# Revit family: ROTHOB_Rothoblaas_Screw_VGZEvo
name_source: partatom
category: Collegamenti strutturali
units: mm (PartAtom-declared; Revit-internal decimal feet)

## family parameters
Attiva taglio nelle viste = Sì
Condiviso = No
Host = Superficie
Materiale per comportamento modello = Acciaio
Numero OmniClass = 23.13.23.11.19.13
Taglio con vuoti quando caricato = No
Titolo OmniClass = Wood Connectors

## types (44) — shared parameters
CECode = ETA-11/0030
Category = Pr_20_29_76_75: Self-tapping screws
CodePerformance = CE - Construction products
Color = Silver
Description = Fully threaded screw with cylindrical head
DurationUnit = Years
Esporta tipo in formato IFC con nome = IfcMechanicalFastenerType
ExpectedLife = 50
Features = Self-tapping screws for timber constructions
Finish = C4 EVO coating
HeadThickness = 7.2 mm  [stored 0.023622 ft]
ICC-ESCode = AC233 | AC257 ESR-4645
IfcExportAs = IfcMechanicalFastenerType
IfcExportType = USERDEFINED
ManufacturerName = ROTHO BLAAS SRL
ManufacturerURL = www.rothoblaas.com
Material = Carbon steel
ModelDisclaimer = The latest version of the data sheets can be found on our website
Name = Screw
ObjectMaterial = ROTHOB_Rothoblaas_CarbonSteel_C4EvoCoating
OmniClassCode = 23-13 23 11 19 13
OmniClassTitle = Wood Connectors
OmniClassVersion = 2012-05-16
ProductInformation = https://www.rothoblaas.com
Prospetto di default = 1219.2 mm
Shape = Cylindrical
Tipo IFC predefinito = USERDEFINED
UKCACode = UKTA-0836 22/6195
UniClass2015Code = Pr_20_29_76_75
UniClass2015Title = Self-tapping screws
UniClass2015Version = Products v1.30
Version = 1

## per-type parameters (varying)
| type | BitType | HeadDiameter_dk | InnerHeadDiameter | InsertionLength_L | MinWeight | ModelNumber | ModelNumberCode | NominalDiameter | NominalDiameter_d1 | NominalLength | Size | ThreadDiameter_d2 | ThreadLength_b | ThreadRadius | TipLength | UnderheadDiameter |
| 05.3x080mm | 25 | 8 mm  [stored 0.0262467 ft] | 4 mm  [stored 0.0131234 ft] | 80 mm | 0.01 kg | VGZEVO580 | 580 | 5.3 mm  [stored 0.0173885 ft] | 5.3 mm  [stored 0.0173885 ft] | 80 mm | 5.3x80 mm | 3.6 mm  [stored 0.011811 ft] | 70 mm | 1.8 mm  [stored 0.00590551 ft] | 4 mm  [stored 0.0131234 ft] | 7.2 mm  [stored 0.023622 ft] |
| 05.3x100mm | 25 | 8 mm  [stored 0.0262467 ft] | 4 mm  [stored 0.0131234 ft] | 100 mm | 0.008 kg | VGZEVO5100 | 5100 | 5.3 mm  [stored 0.0173885 ft] | 5.3 mm  [stored 0.0173885 ft] | 100 mm | 5.3x100 mm | 3.6 mm  [stored 0.011811 ft] | 90 mm | 1.8 mm  [stored 0.00590551 ft] | 5 mm  [stored 0.0164042 ft] | 7.2 mm  [stored 0.023622 ft] |
| 05.3x120mm | 25 | 8 mm  [stored 0.0262467 ft] | 4 mm  [stored 0.0131234 ft] | 120 mm | 0.010 kg | VGZEVO5120 | 5120 | 5.3 mm  [stored 0.0173885 ft] | 5.3 mm  [stored 0.0173885 ft] | 120 mm | 5.3x120 mm | 3.6 mm  [stored 0.011811 ft] | 110 mm | 1.8 mm  [stored 0.00590551 ft] | 6 mm  [stored 0.019685 ft] | 7.2 mm  [stored 0.023622 ft] |
| 05.6x140mm | 25 | 8 mm  [stored 0.0262467 ft] | 4 mm  [stored 0.0131234 ft] | 140 mm | 0.016 kg | VGZEVO5140 | 5140 | 5.6 mm  [stored 0.0183727 ft] | 5.6 mm  [stored 0.0183727 ft] | 140 mm | 5.6x140 mm | 3.8 mm | 130 mm | 1.9 mm | 7 mm  [stored 0.0229659 ft] | 7.2 mm  [stored 0.023622 ft] |
| 05.6x150mm | 25 | 8 mm  [stored 0.0262467 ft] | 4 mm  [stored 0.0131234 ft] | 150 mm | 0.018 kg | VGZEVO5150 | 5150 | 5.6 mm  [stored 0.0183727 ft] | 5.6 mm  [stored 0.0183727 ft] | 150 mm | 5.6x150 mm | 3.8 mm | 140 mm | 1.9 mm | 7.5 mm  [stored 0.0246063 ft] | 7.2 mm  [stored 0.023622 ft] |
| 05.6x160mm | 25 | 8 mm  [stored 0.0262467 ft] | 4 mm  [stored 0.0131234 ft] | 160 mm | 0.018 kg | VGZEVO5160 | 5160 | 5.6 mm  [stored 0.0183727 ft] | 5.6 mm  [stored 0.0183727 ft] | 160 mm | 5.6x160 mm | 3.8 mm | 150 mm | 1.9 mm | 8 mm  [stored 0.0262467 ft] | 7.2 mm  [stored 0.023622 ft] |
| 07x080mm | 30 | 9.5 mm  [stored 0.031168 ft] | 4.75 mm  [stored 0.015584 ft] | 80 mm | 0.015 kg | VGZEVO780 | 780 | 7 mm  [stored 0.0229659 ft] | 7 mm  [stored 0.0229659 ft] | 80 mm | 7x80 mm | 4.6 mm  [stored 0.0150919 ft] | 70 mm | 2.3 mm  [stored 0.00754593 ft] | 4 mm  [stored 0.0131234 ft] | 8.55 mm |
| 07x100mm | 30 | 9.5 mm  [stored 0.031168 ft] | 4.75 mm  [stored 0.015584 ft] | 100 mm | 0.019 kg | VGZEVO7100 | 7100 | 7 mm  [stored 0.0229659 ft] | 7 mm  [stored 0.0229659 ft] | 100 mm | 7x100 mm | 4.6 mm  [stored 0.0150919 ft] | 90 mm | 2.3 mm  [stored 0.00754593 ft] | 5 mm  [stored 0.0164042 ft] | 8.55 mm |
| 07x120mm | 30 | 9.5 mm  [stored 0.031168 ft] | 4.75 mm  [stored 0.015584 ft] | 120 mm | 0.016 kg | VGZEVO7120 | 7120 | 7 mm  [stored 0.0229659 ft] | 7 mm  [stored 0.0229659 ft] | 120 mm | 7x120 mm | 4.6 mm  [stored 0.0150919 ft] | 110 mm | 2.3 mm  [stored 0.00754593 ft] | 6 mm  [stored 0.019685 ft] | 8.55 mm |
| 07x140mm | 30 | 9.5 mm  [stored 0.031168 ft] | 4.75 mm  [stored 0.015584 ft] | 140 mm | 0.022 kg | VGZEVO7140 | 7140 | 7 mm  [stored 0.0229659 ft] | 7 mm  [stored 0.0229659 ft] | 140 mm | 7x140 mm | 4.6 mm  [stored 0.0150919 ft] | 130 mm | 2.3 mm  [stored 0.00754593 ft] | 7 mm  [stored 0.0229659 ft] | 8.55 mm |
| 07x160mm | 30 | 9.5 mm  [stored 0.031168 ft] | 4.75 mm  [stored 0.015584 ft] | 160 mm | 0.023 kg | VGZEVO7160 | 7160 | 7 mm  [stored 0.0229659 ft] | 7 mm  [stored 0.0229659 ft] | 160 mm | 7x160 mm | 4.6 mm  [stored 0.0150919 ft] | 150 mm | 2.3 mm  [stored 0.00754593 ft] | 8 mm  [stored 0.0262467 ft] | 8.55 mm |
| 07x180mm | 30 | 9.5 mm  [stored 0.031168 ft] | 4.75 mm  [stored 0.015584 ft] | 180 mm | 0.028 kg | VGZEVO7180 | 7180 | 7 mm  [stored 0.0229659 ft] | 7 mm  [stored 0.0229659 ft] | 180 mm | 7x180 mm | 4.6 mm  [stored 0.0150919 ft] | 170 mm | 2.3 mm  [stored 0.00754593 ft] | 9 mm  [stored 0.0295276 ft] | 8.55 mm |
| 07x200mm | 30 | 9.5 mm  [stored 0.031168 ft] | 4.75 mm  [stored 0.015584 ft] | 200 mm | 0.031 kg | VGZEVO7200 | 7200 | 7 mm  [stored 0.0229659 ft] | 7 mm  [stored 0.0229659 ft] | 200 mm | 7x200 mm | 4.6 mm  [stored 0.0150919 ft] | 190 mm | 2.3 mm  [stored 0.00754593 ft] | 10 mm  [stored 0.0328084 ft] | 8.55 mm |
| 07x220mm | 30 | 9.5 mm  [stored 0.031168 ft] | 4.75 mm  [stored 0.015584 ft] | 220 mm | 0.035 kg | VGZEVO7220 | 7220 | 7 mm  [stored 0.0229659 ft] | 7 mm  [stored 0.0229659 ft] | 220 mm | 7x220 mm | 4.6 mm  [stored 0.0150919 ft] | 210 mm | 2.3 mm  [stored 0.00754593 ft] | 11 mm  [stored 0.0360892 ft] | 8.55 mm |
| 07x240mm | 30 | 9.5 mm  [stored 0.031168 ft] | 4.75 mm  [stored 0.015584 ft] | 240 mm | 0.036 kg | VGZEVO7240 | 7240 | 7 mm  [stored 0.0229659 ft] | 7 mm  [stored 0.0229659 ft] | 240 mm | 7x240 mm | 4.6 mm  [stored 0.0150919 ft] | 230 mm | 2.3 mm  [stored 0.00754593 ft] | 12 mm  [stored 0.0393701 ft] | 8.55 mm |
| 07x260mm | 30 | 9.5 mm  [stored 0.031168 ft] | 4.75 mm  [stored 0.015584 ft] | 260 mm | 0.035 kg | VGZEVO7260 | 7260 | 7 mm  [stored 0.0229659 ft] | 7 mm  [stored 0.0229659 ft] | 260 mm | 7x260 mm | 4.6 mm  [stored 0.0150919 ft] | 250 mm | 2.3 mm  [stored 0.00754593 ft] | 13 mm | 8.55 mm |
| 07x280mm | 30 | 9.5 mm  [stored 0.031168 ft] | 4.75 mm  [stored 0.015584 ft] | 280 mm | 0.041 kg | VGZEVO7280 | 7280 | 7 mm  [stored 0.0229659 ft] | 7 mm  [stored 0.0229659 ft] | 280 mm | 7x280 mm | 4.6 mm  [stored 0.0150919 ft] | 270 mm | 2.3 mm  [stored 0.00754593 ft] | 14 mm  [stored 0.0459318 ft] | 8.55 mm |
| 07x300mm | 30 | 9.5 mm  [stored 0.031168 ft] | 4.75 mm  [stored 0.015584 ft] | 300 mm | 0.046 kg | VGZEVO7300 | 7300 | 7 mm  [stored 0.0229659 ft] | 7 mm  [stored 0.0229659 ft] | 300 mm | 7x300 mm | 4.6 mm  [stored 0.0150919 ft] | 290 mm | 2.3 mm  [stored 0.00754593 ft] | 15 mm  [stored 0.0492126 ft] | 8.55 mm |
| 07x340mm | 30 | 9.5 mm  [stored 0.031168 ft] | 4.75 mm  [stored 0.015584 ft] | 340 mm | 0.098 kg | VGZEVO7340 | 7340 | 7 mm  [stored 0.0229659 ft] | 7 mm  [stored 0.0229659 ft] | 340 mm | 7x340 mm | 4.6 mm  [stored 0.0150919 ft] | 330 mm | 2.3 mm  [stored 0.00754593 ft] | 17 mm | 8.55 mm |
| 07x380mm | 30 | 9.5 mm  [stored 0.031168 ft] | 4.75 mm  [stored 0.015584 ft] | 380 mm | 0.046 kg | VGZEVO7380 | 7380 | 7 mm  [stored 0.0229659 ft] | 7 mm  [stored 0.0229659 ft] | 380 mm | 7x380 mm | 4.6 mm  [stored 0.0150919 ft] | 370 mm | 2.3 mm  [stored 0.00754593 ft] | 19 mm | 8.55 mm |
| 09x160mm | 40 | 11.5 mm  [stored 0.0377297 ft] | 5.75 mm  [stored 0.0188648 ft] | 160 mm | 0.045 kg | VGZEVO9160 | 9160 | 9 mm  [stored 0.0295276 ft] | 9 mm  [stored 0.0295276 ft] | 160 mm | 9x160 mm | 5.9 mm  [stored 0.019357 ft] | 150 mm | 2.95 mm  [stored 0.00967848 ft] | 8 mm  [stored 0.0262467 ft] | 10.35 mm |
| 09x180mm | 40 | 11.5 mm  [stored 0.0377297 ft] | 5.75 mm  [stored 0.0188648 ft] | 180 mm | 0.05 kg | VGZEVO9180 | 9180 | 9 mm  [stored 0.0295276 ft] | 9 mm  [stored 0.0295276 ft] | 180 mm | 9x180 mm | 5.9 mm  [stored 0.019357 ft] | 170 mm | 2.95 mm  [stored 0.00967848 ft] | 9 mm  [stored 0.0295276 ft] | 10.35 mm |
| 09x200mm | 40 | 11.5 mm  [stored 0.0377297 ft] | 5.75 mm  [stored 0.0188648 ft] | 200 mm | 0.051 kg | VGZEVO9200 | 9200 | 9 mm  [stored 0.0295276 ft] | 9 mm  [stored 0.0295276 ft] | 200 mm | 9x200 mm | 5.9 mm  [stored 0.019357 ft] | 190 mm | 2.95 mm  [stored 0.00967848 ft] | 10 mm  [stored 0.0328084 ft] | 10.35 mm |
| 09x220mm | 40 | 11.5 mm  [stored 0.0377297 ft] | 5.75 mm  [stored 0.0188648 ft] | 220 mm | 0.060 kg | VGZEVO9220 | 9220 | 9 mm  [stored 0.0295276 ft] | 9 mm  [stored 0.0295276 ft] | 220 mm | 9x220 mm | 5.9 mm  [stored 0.019357 ft] | 210 mm | 2.95 mm  [stored 0.00967848 ft] | 11 mm  [stored 0.0360892 ft] | 10.35 mm |
| 09x240mm | 40 | 11.5 mm  [stored 0.0377297 ft] | 5.75 mm  [stored 0.0188648 ft] | 240 mm | 0.061 kg | VGZEVO9240 | 9240 | 9 mm  [stored 0.0295276 ft] | 9 mm  [stored 0.0295276 ft] | 240 mm | 9x240 mm | 5.9 mm  [stored 0.019357 ft] | 230 mm | 2.95 mm  [stored 0.00967848 ft] | 12 mm  [stored 0.0393701 ft] | 10.35 mm |
| 09x260mm | 40 | 11.5 mm  [stored 0.0377297 ft] | 5.75 mm  [stored 0.0188648 ft] | 260 mm | 0.069 kg | VGZEVO9260 | 9260 | 9 mm  [stored 0.0295276 ft] | 9 mm  [stored 0.0295276 ft] | 260 mm | 9x260 mm | 5.9 mm  [stored 0.019357 ft] | 250 mm | 2.95 mm  [stored 0.00967848 ft] | 13 mm | 10.35 mm |
| 09x280mm | 40 | 11.5 mm  [stored 0.0377297 ft] | 5.75 mm  [stored 0.0188648 ft] | 280 mm | 0.072 kg | VGZEVO9280 | 9280 | 9 mm  [stored 0.0295276 ft] | 9 mm  [stored 0.0295276 ft] | 280 mm | 9x280 mm | 5.9 mm  [stored 0.019357 ft] | 270 mm | 2.95 mm  [stored 0.00967848 ft] | 14 mm  [stored 0.0459318 ft] | 10.35 mm |
| 09x300mm | 40 | 11.5 mm  [stored 0.0377297 ft] | 5.75 mm  [stored 0.0188648 ft] | 300 mm | 0.073 kg | VGZEVO9300 | 9300 | 9 mm  [stored 0.0295276 ft] | 9 mm  [stored 0.0295276 ft] | 300 mm | 9x300 mm | 5.9 mm  [stored 0.019357 ft] | 290 mm | 2.95 mm  [stored 0.00967848 ft] | 15 mm  [stored 0.0492126 ft] | 10.35 mm |
| 09x320mm | 40 | 11.5 mm  [stored 0.0377297 ft] | 5.75 mm  [stored 0.0188648 ft] | 320 mm | 0.082 kg | VGZEVO9320 | 9320 | 9 mm  [stored 0.0295276 ft] | 9 mm  [stored 0.0295276 ft] | 320 mm | 9x320 mm | 5.9 mm  [stored 0.019357 ft] | 310 mm | 2.95 mm  [stored 0.00967848 ft] | 16 mm  [stored 0.0524934 ft] | 10.35 mm |
| 09x340mm | 40 | 11.5 mm  [stored 0.0377297 ft] | 5.75 mm  [stored 0.0188648 ft] | 340 mm | 0.098 kg | VGZEVO9340 | 9340 | 9 mm  [stored 0.0295276 ft] | 9 mm  [stored 0.0295276 ft] | 340 mm | 9x340 mm | 5.9 mm  [stored 0.019357 ft] | 330 mm | 2.95 mm  [stored 0.00967848 ft] | 17 mm | 10.35 mm |
| 09x360mm | 40 | 11.5 mm  [stored 0.0377297 ft] | 5.75 mm  [stored 0.0188648 ft] | 360 mm | 0.090 kg | VGZEVO9360 | 9360 | 9 mm  [stored 0.0295276 ft] | 9 mm  [stored 0.0295276 ft] | 360 mm | 9x360 mm | 5.9 mm  [stored 0.019357 ft] | 350 mm | 2.95 mm  [stored 0.00967848 ft] | 18 mm  [stored 0.0590551 ft] | 10.35 mm |
| 09x380mm | 40 | 11.5 mm  [stored 0.0377297 ft] | 5.75 mm  [stored 0.0188648 ft] | 380 mm | 0.095 kg | VGZEVO9380 | 9380 | 9 mm  [stored 0.0295276 ft] | 9 mm  [stored 0.0295276 ft] | 380 mm | 9x380 mm | 5.9 mm  [stored 0.019357 ft] | 370 mm | 2.95 mm  [stored 0.00967848 ft] | 19 mm | 10.35 mm |
| 09x400mm | 40 | 11.5 mm  [stored 0.0377297 ft] | 5.75 mm  [stored 0.0188648 ft] | 400 mm | 0.107 kg | VGZEVO9400 | 9400 | 9 mm  [stored 0.0295276 ft] | 9 mm  [stored 0.0295276 ft] | 400 mm | 9x400 mm | 5.9 mm  [stored 0.019357 ft] | 390 mm | 2.95 mm  [stored 0.00967848 ft] | 20 mm | 10.35 mm |
| 09x440mm | 40 | 11.5 mm  [stored 0.0377297 ft] | 5.75 mm  [stored 0.0188648 ft] | 440 mm | 0.119 kg | VGZEVO9440 | 9440 | 9 mm  [stored 0.0295276 ft] | 9 mm  [stored 0.0295276 ft] | 440 mm | 9x440 mm | 5.9 mm  [stored 0.019357 ft] | 430 mm | 2.95 mm  [stored 0.00967848 ft] | 22 mm | 10.35 mm |
| 09x480mm | 40 | 11.5 mm  [stored 0.0377297 ft] | 5.75 mm  [stored 0.0188648 ft] | 480 mm | 0.128 kg | VGZEVO9480 | 9480 | 9 mm  [stored 0.0295276 ft] | 9 mm  [stored 0.0295276 ft] | 480 mm | 9x480 mm | 5.9 mm  [stored 0.019357 ft] | 470 mm | 2.95 mm  [stored 0.00967848 ft] | 24 mm | 10.35 mm |
| 09x520mm | 40 | 11.5 mm  [stored 0.0377297 ft] | 5.75 mm  [stored 0.0188648 ft] | 520 mm | 0.142 kg | VGZEVO9520 | 9520 | 9 mm  [stored 0.0295276 ft] | 9 mm  [stored 0.0295276 ft] | 520 mm | 9x520 mm | 5.9 mm  [stored 0.019357 ft] | 510 mm | 2.95 mm  [stored 0.00967848 ft] | 26 mm | 10.35 mm |
| 11x250mm | 50 | 13.5 mm  [stored 0.0442913 ft] | 6.75 mm  [stored 0.0221457 ft] | 250 mm | 0.089 kg | VGZEVO11250 | 11250 | 11 mm  [stored 0.0360892 ft] | 11 mm  [stored 0.0360892 ft] | 250 mm | 11x250 mm | 6.6 mm  [stored 0.0216535 ft] | 240 mm | 3.3 mm  [stored 0.0108268 ft] | 12.5 mm  [stored 0.0410105 ft] | 12.15 mm  [stored 0.0398622 ft] |
| 11x300mm | 50 | 13.5 mm  [stored 0.0442913 ft] | 6.75 mm  [stored 0.0221457 ft] | 300 mm | 0.107 kg | VGZEVO11300 | 11300 | 11 mm  [stored 0.0360892 ft] | 11 mm  [stored 0.0360892 ft] | 300 mm | 11x300 mm | 6.6 mm  [stored 0.0216535 ft] | 290 mm | 3.3 mm  [stored 0.0108268 ft] | 15 mm  [stored 0.0492126 ft] | 12.15 mm  [stored 0.0398622 ft] |
| 11x350mm | 50 | 13.5 mm  [stored 0.0442913 ft] | 6.75 mm  [stored 0.0221457 ft] | 350 mm | 0.124 kg | VGZEVO11350 | 11350 | 11 mm  [stored 0.0360892 ft] | 11 mm  [stored 0.0360892 ft] | 350 mm | 11x350 mm | 6.6 mm  [stored 0.0216535 ft] | 340 mm | 3.3 mm  [stored 0.0108268 ft] | 17.5 mm | 12.15 mm  [stored 0.0398622 ft] |
| 11x400mm | 50 | 13.5 mm  [stored 0.0442913 ft] | 6.75 mm  [stored 0.0221457 ft] | 400 mm | 0.142 kg | VGZEVO11400 | 11400 | 11 mm  [stored 0.0360892 ft] | 11 mm  [stored 0.0360892 ft] | 400 mm | 11x400 mm | 6.6 mm  [stored 0.0216535 ft] | 390 mm | 3.3 mm  [stored 0.0108268 ft] | 20 mm | 12.15 mm  [stored 0.0398622 ft] |
| 11x450mm | 50 | 13.5 mm  [stored 0.0442913 ft] | 6.75 mm  [stored 0.0221457 ft] | 450 mm | 0.098 kg | VGZEVO11450 | 11450 | 11 mm  [stored 0.0360892 ft] | 11 mm  [stored 0.0360892 ft] | 450 mm | 11x450 mm | 6.6 mm  [stored 0.0216535 ft] | 440 mm | 3.3 mm  [stored 0.0108268 ft] | 22.5 mm | 12.15 mm  [stored 0.0398622 ft] |
| 11x500mm | 50 | 13.5 mm  [stored 0.0442913 ft] | 6.75 mm  [stored 0.0221457 ft] | 500 mm | 0.179 kg | VGZEVO11500 | 11500 | 11 mm  [stored 0.0360892 ft] | 11 mm  [stored 0.0360892 ft] | 500 mm | 11x500 mm | 6.6 mm  [stored 0.0216535 ft] | 490 mm | 3.3 mm  [stored 0.0108268 ft] | 25 mm | 12.15 mm  [stored 0.0398622 ft] |
| 11x550mm | 50 | 13.5 mm  [stored 0.0442913 ft] | 6.75 mm  [stored 0.0221457 ft] | 550 mm | 0.196 kg | VGZEVO11550 | 11550 | 11 mm  [stored 0.0360892 ft] | 11 mm  [stored 0.0360892 ft] | 550 mm | 11x550 mm | 6.6 mm  [stored 0.0216535 ft] | 540 mm | 3.3 mm  [stored 0.0108268 ft] | 27.5 mm | 12.15 mm  [stored 0.0398622 ft] |
| 11x600mm | 50 | 13.5 mm  [stored 0.0442913 ft] | 6.75 mm  [stored 0.0221457 ft] | 600 mm | 0.212 kg | VGZEVO11600 | 11600 | 11 mm  [stored 0.0360892 ft] | 11 mm  [stored 0.0360892 ft] | 600 mm | 11x600 mm | 6.6 mm  [stored 0.0216535 ft] | 590 mm | 3.3 mm  [stored 0.0108268 ft] | 30 mm | 12.15 mm  [stored 0.0398622 ft] |

note: [stored X ft] marks values corroborated as IEEE doubles in the binary element streams (Revit-internal decimal feet)
